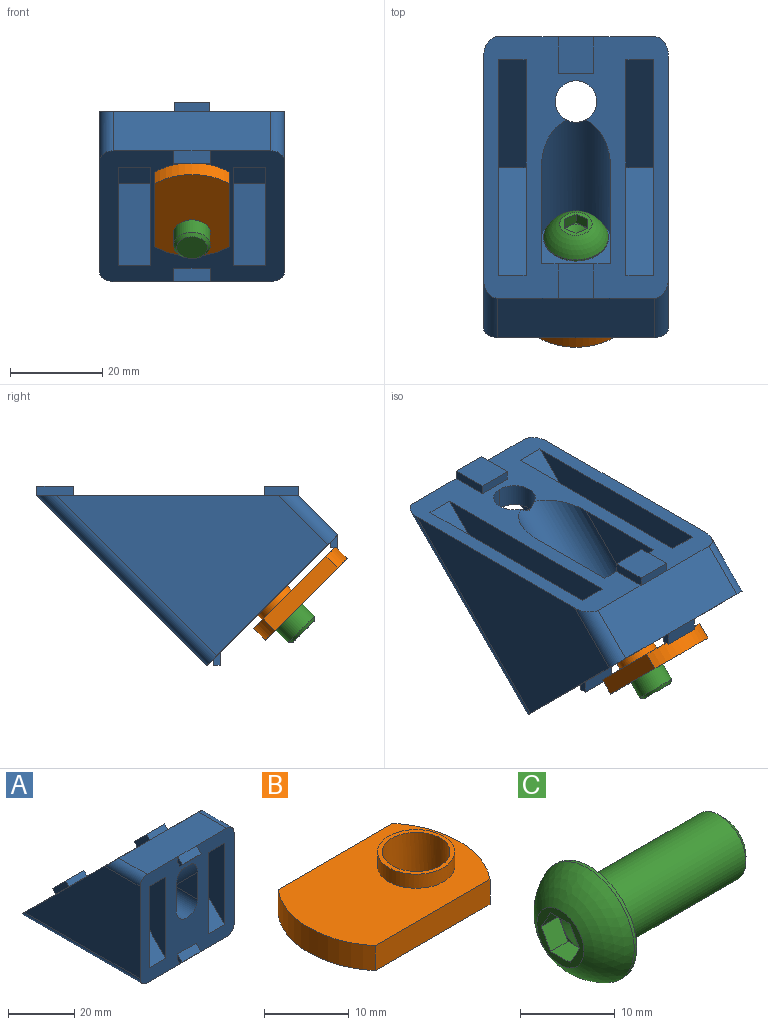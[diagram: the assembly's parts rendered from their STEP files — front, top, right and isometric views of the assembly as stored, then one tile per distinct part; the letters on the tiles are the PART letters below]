
ASSEMBLY  parts=3 mates=2
PART A: 65 faces, bbox 40x55.6x46.7 mm
  f0: plane 7.7x5.25mm, normal (0,0.71,0.71), area 57.2mm2, adj f2,f14,f18,f19
  f1: plane 8x1.06mm, normal (0,-0.71,-0.71), area 12mm2, adj f29,f30,f31,f32
  f2: plane 7.7x1.41mm, normal (0,-0.71,0.71), area 15.4mm2, adj f0,f14,f18,f36
  f3: plane 8x1.06mm, normal (0,-0.71,-0.71), area 12mm2, adj f4,f37,f38,f39
  f4: plane 8x2mm, normal (0,-0.71,0.71), area 22.6mm2, adj f3,f36,f37,f39
  f5: plane 17.5x7mm, normal (0,-1,0), area 122.5mm2, adj f40,f41,f42,f43
  f6: plane 17.5x7mm, normal (0,-1,0), area 122.5mm2, adj f44,f45,f46,f47
  f7: cylinder r=4.5mm len=2.03mm, axis (0,1,0), area 0.2mm2, adj f8,f51
  f8: plane 15x15mm, normal (0,1,0), area 135.3mm2, adj f7,f12,f13,f19,f20,f48,f50,f51
  f9: plane 7.7x5.66mm, normal (0,0.71,0.71), area 61.6mm2, adj f15,f16,f17,f59
  f10: cylinder r=4.5mm len=9.9mm, axis (0,-0.71,-0.71), area 69.6mm2, adj f11,f12,f58,f60
  f11: cylinder r=4.5mm len=9.9mm, axis (0,-0.71,-0.71), area 69.6mm2, adj f10,f12,f58,f60
  f12: cylinder r=7.5mm len=29.24mm, axis (0,1,0), area 627.8mm2, adj f8,f10,f11,f13,f20,f60
  f13: plane 22x14.75mm, normal (1,0,0), area 189.4mm2, adj f8,f12,f19,f60
  f14: plane 6.66x6.66mm, normal (-1,0,0), area 14.8mm2, adj f0,f2,f19,f60
  f15: plane 7.07x7.07mm, normal (-1,0,0), area 16mm2, adj f9,f16,f59,f60
  f16: plane 7.7x1.41mm, normal (0,-0.71,0.71), area 15.4mm2, adj f9,f15,f17,f60
  f17: plane 7.07x7.07mm, normal (1,0,0), area 16mm2, adj f9,f16,f59,f60
  f18: plane 6.66x6.66mm, normal (1,0,0), area 14.8mm2, adj f0,f2,f19,f60
  f19: plane 15x8.66mm, normal (0,0.71,-0.71), area 169.2mm2, adj f0,f8,f13,f14,f18,f20,f60
  f20: plane 22x14.75mm, normal (-1,0,0), area 189.4mm2, adj f8,f12,f19,f60
  f21: plane 33x6mm, normal (0,0,1), area 198mm2, adj f22,f23,f24,f60
  f22: plane 33x33mm, normal (1,0,0), area 544.5mm2, adj f21,f23,f60
  f23: plane 33x6mm, normal (0,1,0), area 198mm2, adj f21,f22,f24,f60
  f24: plane 33x33mm, normal (-1,0,0), area 544.5mm2, adj f21,f23,f60
  f25: plane 33x6mm, normal (0,0,1), area 198mm2, adj f26,f27,f28,f60
  f26: plane 33x33mm, normal (1,0,0), area 544.5mm2, adj f25,f27,f60
  f27: plane 33x6mm, normal (0,1,0), area 198mm2, adj f25,f26,f28,f60
  f28: plane 33x33mm, normal (-1,0,0), area 544.5mm2, adj f25,f27,f60
  f29: plane 3.06x2mm, normal (-1,0,0), area 3.1mm2, adj f1,f30,f32,f62
  f30: plane 8x0.94mm, normal (0,0.71,-0.71), area 10.6mm2, adj f1,f29,f31,f62
  f31: plane 3.06x2mm, normal (1,0,0), area 3.1mm2, adj f1,f30,f32,f62
  f32: plane 8x2mm, normal (0,-0.71,0.71), area 22.6mm2, adj f1,f29,f31,f62
  f33: cylinder r=3mm len=15mm, axis (0,1,0), area 61.7mm2, adj f34,f36,f60,f62
  f34: plane 49x34mm, normal (1,0,0), area 1088mm2, adj f33,f60,f61,f62
  f35: cylinder r=3mm len=15mm, axis (0,1,0), area 61.7mm2, adj f36,f54,f60,f62
  f36: plane 34x12mm, normal (0,0,1), area 408mm2, adj f2,f4,f33,f35,f60,f62
  f37: plane 3.06x2mm, normal (-1,0,0), area 3.1mm2, adj f3,f4,f38,f62
  f38: plane 8x0.94mm, normal (0,0.71,-0.71), area 10.6mm2, adj f3,f37,f39,f62
  f39: plane 3.06x2mm, normal (1,0,0), area 3.1mm2, adj f3,f4,f38,f62
  f40: plane 30x12.5mm, normal (1,0,0), area 296.9mm2, adj f5,f41,f43,f62
  f41: plane 12.5x12.5mm, normal (0,-0.71,0.71), area 123.7mm2, adj f5,f40,f42,f62
  f42: plane 30x12.5mm, normal (-1,0,0), area 296.9mm2, adj f5,f41,f43,f62
  f43: plane 12.5x7mm, normal (0,0,-1), area 87.5mm2, adj f5,f40,f42,f62
  f44: plane 30x12.5mm, normal (1,0,0), area 296.9mm2, adj f6,f45,f47,f62
  f45: plane 12.5x12.5mm, normal (0,-0.71,0.71), area 123.7mm2, adj f6,f44,f46,f62
  f46: plane 30x12.5mm, normal (-1,0,0), area 296.9mm2, adj f6,f45,f47,f62
  f47: plane 12.5x7mm, normal (0,0,-1), area 87.5mm2, adj f6,f44,f46,f62
  f48: cylinder r=4.5mm len=10mm, axis (0,1,0), area 141.4mm2, adj f8,f49,f53,f62
  f49: plane 10x10mm, normal (-1,0,0), area 50mm2, adj f48,f50,f62
  f50: cylinder r=3.1mm len=14.38mm, axis (0,-0.71,0.71), area 68.9mm2, adj f8,f49,f51,f62
  f51: plane 10x10mm, normal (0,-0.71,-0.71), area 39.4mm2, adj f7,f8,f50,f52,f62
  f52: cylinder r=3.1mm len=14.38mm, axis (0,-0.71,0.71), area 68.9mm2, adj f8,f51,f53,f62
  f53: plane 10x10mm, normal (1,0,0), area 50mm2, adj f48,f52,f62
  f54: plane 49x34mm, normal (-1,0,0), area 1088mm2, adj f35,f60,f62,f63
  f55: plane 12.73x6.36mm, normal (1,0,0), area 40.5mm2, adj f56,f58,f64
  f56: cylinder r=7.5mm len=16.99mm, axis (0,-0.71,-0.71), area 324.6mm2, adj f55,f57,f58,f64
  f57: plane 12.73x6.36mm, normal (-1,0,0), area 40.5mm2, adj f56,f58,f64
  f58: plane 15x11.67mm, normal (0,-0.71,-0.71), area 159.7mm2, adj f10,f11,f55,f56,f57,f64
  f59: plane 7.7x1.41mm, normal (0,0.71,-0.71), area 15.4mm2, adj f9,f15,f17,f64
  f60: plane 40x40mm, normal (0,0.71,0.71), area 1073.7mm2, adj f10,f11,f12,f13,f14,f15,f16,f17
  f61: cylinder r=3mm len=52mm, axis (0,1,0), area 239.9mm2, adj f34,f60,f62,f64
  f62: plane 40x40mm, normal (0,-1,0), area 982.9mm2, adj f29,f30,f31,f32,f33,f34,f35,f36
  f63: cylinder r=3mm len=52mm, axis (0,1,0), area 239.9mm2, adj f54,f60,f62,f64
  f64: plane 52x34mm, normal (0,0,-1), area 1452.1mm2, adj f55,f56,f57,f58,f59,f60,f61,f62
PART B: 9 faces, bbox 25x16.2x5.6 mm
  f0: cylinder r=12.7mm len=16.19mm, axis (0,0,1), area 63.3mm2, adj f1,f3,f4,f5
  f1: plane 19.16x3.61mm, normal (0,-1,0), area 69.1mm2, adj f0,f2,f4,f5
  f2: cylinder r=12.7mm len=16.19mm, axis (0,0,1), area 63.3mm2, adj f1,f3,f4,f5
  f3: plane 19.16x3.61mm, normal (0,1,0), area 69.1mm2, adj f0,f2,f4,f5
  f4: plane 24.99x16.19mm, normal (0,0,-1), area 324.6mm2, adj f0,f1,f2,f3,f8
  f5: plane 24.99x16.19mm, normal (0,0,1), area 309.5mm2, adj f0,f1,f2,f3,f6
  f6: cylinder r=4.56mm len=9.12mm, axis (0,0,-1), area 58.2mm2, adj f5,f7
  f7: plane 9.12x9.12mm, normal (0,0,1), area 15mm2, adj f6,f8
  f8: cylinder r=4mm len=8mm, axis (0,0,-1), area 141.7mm2, adj f4,f7
PART C: 21 faces, bbox 24.4x14x14 mm
  f0: plane 7x7mm, normal (-1,0,0), area 16.8mm2, adj f1,f8,f9,f10,f11,f12,f13
  f1: sphere r=7.45mm, area 188.3mm2, adj f0,f2
  f2: cylinder r=7mm len=14mm, axis (-1,0,0), area 16.7mm2, adj f1,f3
  f3: plane 14x14mm, normal (1,0,0), area 93.1mm2, adj f2,f7
  f4: cylinder r=4mm len=18.91mm, axis (-1,0,0), area 475.2mm2, adj f5,f7
  f5: cone r=3.31mm half-angle=45deg, axis (-1,0,0), area 22.4mm2, adj f4,f6
  f6: plane 6.62x6.62mm, normal (1,0,0), area 34.4mm2, adj f5
  f7: torus R=4.4mm, axis (-1,0,0), area 16.4mm2, adj f3,f4
  f8: plane 2.6x2.5mm, normal (0,0.87,-0.5), area 7.5mm2, adj f0,f9,f13,f18,f19
  f9: plane 2.6x2.5mm, normal (0,0.87,0.5), area 7.5mm2, adj f0,f8,f10,f17,f18
  f10: plane 2.89x2.6mm, normal (0,0,1), area 7.5mm2, adj f0,f9,f11,f16,f17
  f11: plane 2.6x2.5mm, normal (0,-0.87,0.5), area 7.5mm2, adj f0,f10,f12,f15,f16
  f12: plane 2.6x2.5mm, normal (0,-0.87,-0.5), area 7.5mm2, adj f0,f11,f13,f14,f15
  f13: plane 2.89x2.6mm, normal (0,0,-1), area 7.5mm2, adj f0,f8,f12,f14,f19
  f14: plane 2.17x1.25mm, normal (-1,0,0), area 0.3mm2, adj f12,f13,f20
  f15: plane 2.5x0.72mm, normal (-1,0,0), area 0.3mm2, adj f11,f12,f20
  f16: plane 2.17x1.25mm, normal (-1,0,0), area 0.3mm2, adj f10,f11,f20
  f17: plane 2.17x1.25mm, normal (-1,0,0), area 0.3mm2, adj f9,f10,f20
  f18: plane 2.5x0.72mm, normal (-1,0,0), area 0.3mm2, adj f8,f9,f20
  f19: plane 2.17x1.25mm, normal (-1,0,0), area 0.3mm2, adj f8,f13,f20
  f20: cone r=0mm half-angle=60deg, axis (-1,0,0), area 22.7mm2, adj f14,f15,f16,f17,f18,f19
PLACE A rot(axis=(1,0,0),45deg) t=(68.05,-72.91,-80.35)mm
PLACE B rot(axis=(-0.36,0.36,0.86),98.4deg) t=(76.14,-70.19,-87.73)mm
PLACE C rot(axis=(0.68,-0.28,-0.68),148.6deg) t=(68.05,-62.44,-69.89)mm
MATE fastened C.f2 <-> A.f7  axis (0,0.71,0.71) through (68.05,-65.83,-73.28)mm
MATE fastened B.f6 <-> C.f2  axis (0,-0.71,-0.71) through (68.05,-72.52,-79.97)mm
